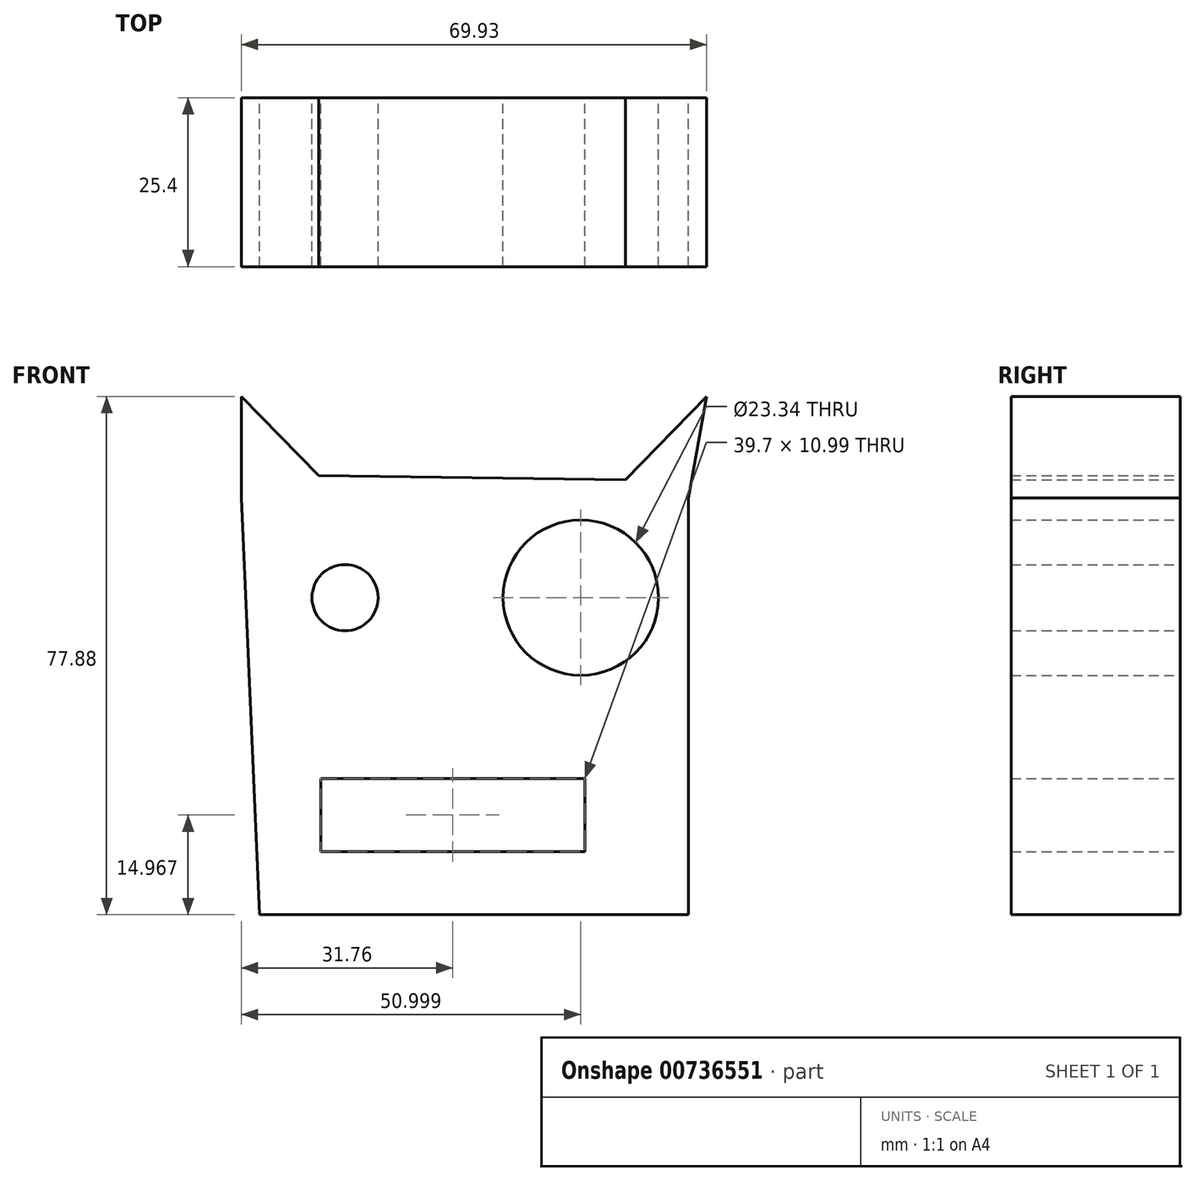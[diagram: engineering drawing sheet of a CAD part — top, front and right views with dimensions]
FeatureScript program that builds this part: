
annotation { "Feature Type Name" : "Feature", "Feature Type Description" : "" }
export const myFeature = defineFeature(function(context is Context, id is Id, definition is map)
    precondition{}
    {
        {
            var Q0;
            Q0=qCreatedBy(makeId("Front.planeOp"),FACE);
            var sketch = newSketch(context, id + "F0", { "sketchPlane" : qUnion([Q0])});
            skLineSegment(sketch, "E0", {"start": v(-26.42, 38.33) * mm, "end": v(-38.02, 50.24) * mm});
            skLineSegment(sketch, "E1", {"start": v(-38.02, 50.24) * mm, "end": v(-38.02, 34.97) * mm});
            skLineSegment(sketch, "E2", {"start": v(-38.02, 34.97) * mm, "end": v(-35.27, -27.64) * mm});
            skLineSegment(sketch, "E3", {"start": v(-35.27, -27.64) * mm, "end": v(29.16, -27.64) * mm});
            skLineSegment(sketch, "E4", {"start": v(29.16, -27.64) * mm, "end": v(29.16, 34.97) * mm});
            skLineSegment(sketch, "E5", {"start": v(29.16, 34.97) * mm, "end": v(31.91, 50.24) * mm});
            skLineSegment(sketch, "E6", {"start": v(31.91, 50.24) * mm, "end": v(19.7, 37.71) * mm});
            skLineSegment(sketch, "E7", {"start": v(19.7, 37.71) * mm, "end": v(-26.42, 38.33) * mm});
            skCircle(sketch, "E8", {"center": v(-22.45, 20) * mm, "radius": 4.97 * mm});
            skCircle(sketch, "E9", {"center": v(12.98, 20) * mm, "radius": 11.67 * mm});
            skLineSegment(sketch, "E10.bottom", {"start": v(-26.11, -7.18) * mm, "end": v(13.59, -7.18) * mm});
            skLineSegment(sketch, "E10.top", {"start": v(-26.11, -18.17) * mm, "end": v(13.59, -18.17) * mm});
            skLineSegment(sketch, "E10.left", {"start": v(-26.11, -7.18) * mm, "end": v(-26.11, -18.17) * mm});
            skLineSegment(sketch, "E10.right", {"start": v(13.59, -7.18) * mm, "end": v(13.59, -18.17) * mm});
            skPoint(sketch, "E10.middle", {"position": v(-6.26, -12.67) * mm});
            skLineSegment(sketch, "E11", {"start": v(-21.22, -7.18) * mm, "end": v(-21.22, -18.17) * mm});
            skLineSegment(sketch, "E12", {"start": v(-21.22, -18.17) * mm, "end": v(-16.34, -18.17) * mm});
            skLineSegment(sketch, "E13", {"start": v(-16.34, -18.17) * mm, "end": v(-16.34, -7.18) * mm});
            skLineSegment(sketch, "E14", {"start": v(-16.34, -7.18) * mm, "end": v(-12.06, -7.18) * mm});
            skLineSegment(sketch, "E15", {"start": v(-12.06, -7.18) * mm, "end": v(-12.06, -18.17) * mm});
            skLineSegment(sketch, "E16", {"start": v(-12.06, -18.17) * mm, "end": v(-6.26, -18.17) * mm});
            skLineSegment(sketch, "E17", {"start": v(-6.26, -18.17) * mm, "end": v(-6.26, -7.18) * mm});
            skLineSegment(sketch, "E18", {"start": v(-6.26, -7.18) * mm, "end": v(-2.9, -7.18) * mm});
            skLineSegment(sketch, "E19", {"start": v(-2.9, -7.18) * mm, "end": v(-2.9, -18.17) * mm});
            skLineSegment(sketch, "E20", {"start": v(-2.9, -18.17) * mm, "end": v(2.3, -18.17) * mm});
            skLineSegment(sketch, "E21", {"start": v(2.3, -18.17) * mm, "end": v(2.3, -7.18) * mm});
            skLineSegment(sketch, "E22", {"start": v(2.3, -7.18) * mm, "end": v(6.26, -7.18) * mm});
            skLineSegment(sketch, "E23", {"start": v(6.26, -7.18) * mm, "end": v(6.26, -18.17) * mm});
            skLineSegment(sketch, "E24", {"start": v(6.26, -18.17) * mm, "end": v(9.31, -18.17) * mm});
            skLineSegment(sketch, "E25", {"start": v(9.31, -18.17) * mm, "end": v(9.31, -7.18) * mm});
            skLineSegment(sketch, "E26", {"start": v(13.59, -12.67) * mm, "end": v(-26.11, -12.67) * mm});
            skSolve(sketch);
        }
        {
            var Q0;
            Q0=makeQuery(id+"F0.imprint","IMPRINT",FACE,{"disambiguationData":[TD([[makeQuery(id+"F0.imprint","IMPRINT",EDGE,{"derivedFrom":sQuery(id+"F0.wireOp",EDGE,"E0")}),1.0]])]});
            extrude(context, id + "F1", {"entities" : qUnion([Q0]), "depth" : 25.4 * mm, "offsetDistance" : 25.4 * mm});
        }
    });
